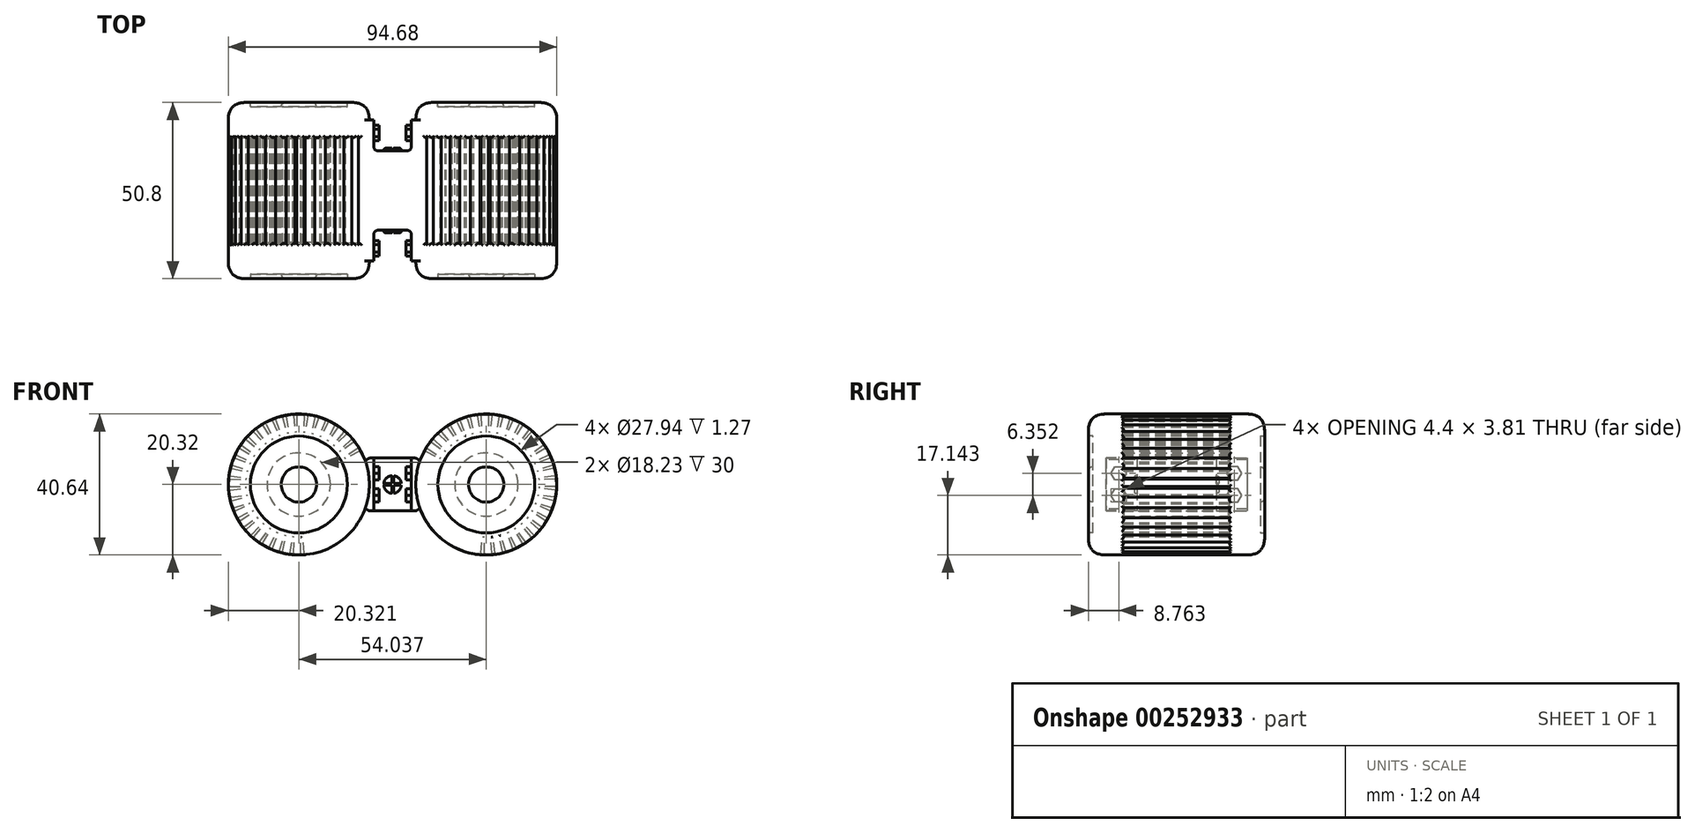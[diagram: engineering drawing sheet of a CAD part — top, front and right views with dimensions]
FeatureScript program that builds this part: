
annotation { "Feature Type Name" : "Feature", "Feature Type Description" : "" }
export const myFeature = defineFeature(function(context is Context, id is Id, definition is map)
    precondition{}
    {
        {
            var Q0;
            Q0=qCreatedBy(makeId("Front.planeOp"),FACE);
            var sketch = newSketch(context, id + "F0", { "sketchPlane" : qUnion([Q0])});
            skArc(sketch, "E0", {"start": v(26.53, 38.5) * mm, "mid": v(31.42, 78.66) * mm, "end": v(18.88, 40.2) * mm});
            skCircle(sketch, "E1", {"center": v(-27.02, 58.82) * mm, "radius": 20.32 * mm});
            skArc(sketch, "E2", {"start": v(18.88, 40.2) * mm, "mid": v(22.62, 38.98) * mm, "end": v(26.53, 38.5) * mm});
            skSolve(sketch);
        }
        {
            var Q0;
            Q0=qSketchRegion(id+"F0",true);
            extrude(context, id + "F1", {"entities" : qUnion([Q0]), "endBound" : BoundingType.SYMMETRIC, "depth" : 50.8 * mm});
        }
        {
            var Q0;
            Q0=qCreatedBy(makeId("Front.planeOp"),FACE);
            var sketch = newSketch(context, id + "F2", { "sketchPlane" : qUnion([Q0])});
            skLineSegment(sketch, "E3.1.0", {"start": v(13.83, 74.28) * mm, "end": v(17.03, 70.33) * mm});
            skLineSegment(sketch, "E3.1.1", {"start": v(13.07, 73.6) * mm, "end": v(16.65, 69.99) * mm});
            skLineSegment(sketch, "E3.1.2", {"start": v(13.07, 73.6) * mm, "end": v(13.83, 74.28) * mm});
            skLineSegment(sketch, "E3.1.3", {"start": v(16.65, 69.99) * mm, "end": v(17.03, 70.33) * mm, "construction": true});
            skLineSegment(sketch, "E3.1.4", {"start": v(16.65, 69.99) * mm, "end": v(17.03, 70.33) * mm});
            skPoint(sketch, "E4", {"position": v(27.02, 58.82) * mm});
            skPoint(sketch, "E5", {"position": v(-27.02, 58.82) * mm});
            skLineSegment(sketch, "E6", {"start": v(27.02, 58.82) * mm, "end": v(13.45, 73.94) * mm, "construction": true});
            skLineSegment(sketch, "E7.1.0", {"start": v(-13.07, 73.6) * mm, "end": v(-16.65, 69.99) * mm});
            skLineSegment(sketch, "E7.1.1", {"start": v(-13.83, 74.28) * mm, "end": v(-17.03, 70.33) * mm});
            skLineSegment(sketch, "E7.1.2", {"start": v(-13.83, 74.28) * mm, "end": v(-13.07, 73.6) * mm});
            skLineSegment(sketch, "E7.1.3", {"start": v(-17.03, 70.33) * mm, "end": v(-16.65, 69.99) * mm, "construction": true});
            skLineSegment(sketch, "E7.1.4", {"start": v(-17.03, 70.33) * mm, "end": v(-16.65, 69.99) * mm});
            skLineSegment(sketch, "E8", {"start": v(-27.02, 58.82) * mm, "end": v(-13.45, 73.94) * mm, "construction": true});
            skLineSegment(sketch, "E9.1.0", {"start": v(11.57, 72.03) * mm, "end": v(15.35, 68.63) * mm});
            skLineSegment(sketch, "E9.1.1", {"start": v(10.93, 71.24) * mm, "end": v(15.03, 68.23) * mm});
            skLineSegment(sketch, "E9.1.2", {"start": v(10.93, 71.24) * mm, "end": v(11.57, 72.03) * mm});
            skLineSegment(sketch, "E9.1.3", {"start": v(15.03, 68.23) * mm, "end": v(15.35, 68.63) * mm, "construction": true});
            skLineSegment(sketch, "E9.1.4", {"start": v(15.03, 68.23) * mm, "end": v(15.35, 68.63) * mm});
            skLineSegment(sketch, "E9.2.0", {"start": v(9.7, 69.45) * mm, "end": v(13.96, 66.68) * mm});
            skLineSegment(sketch, "E9.2.1", {"start": v(9.18, 68.57) * mm, "end": v(13.7, 66.24) * mm});
            skLineSegment(sketch, "E9.2.2", {"start": v(9.18, 68.57) * mm, "end": v(9.7, 69.45) * mm});
            skLineSegment(sketch, "E9.2.3", {"start": v(13.7, 66.24) * mm, "end": v(13.96, 66.68) * mm, "construction": true});
            skLineSegment(sketch, "E9.2.4", {"start": v(13.7, 66.24) * mm, "end": v(13.96, 66.68) * mm});
            skLineSegment(sketch, "E9.15.0", {"start": v(25.41, 38.55) * mm, "end": v(25.94, 43.62) * mm});
            skLineSegment(sketch, "E9.15.1", {"start": v(26.43, 38.5) * mm, "end": v(26.45, 43.59) * mm});
            skLineSegment(sketch, "E9.15.2", {"start": v(26.43, 38.5) * mm, "end": v(25.41, 38.55) * mm});
            skLineSegment(sketch, "E9.15.3", {"start": v(26.45, 43.59) * mm, "end": v(25.94, 43.62) * mm, "construction": true});
            skLineSegment(sketch, "E9.15.4", {"start": v(26.45, 43.59) * mm, "end": v(25.94, 43.62) * mm});
            skLineSegment(sketch, "E9.16.0", {"start": v(28.6, 38.55) * mm, "end": v(28.33, 43.63) * mm});
            skLineSegment(sketch, "E9.16.1", {"start": v(29.61, 38.66) * mm, "end": v(28.84, 43.69) * mm});
            skLineSegment(sketch, "E9.16.2", {"start": v(29.61, 38.66) * mm, "end": v(28.6, 38.55) * mm});
            skLineSegment(sketch, "E9.16.3", {"start": v(28.84, 43.69) * mm, "end": v(28.33, 43.63) * mm, "construction": true});
            skLineSegment(sketch, "E9.16.4", {"start": v(28.84, 43.69) * mm, "end": v(28.33, 43.63) * mm});
            skLineSegment(sketch, "E9.17.0", {"start": v(31.75, 39.05) * mm, "end": v(30.7, 44.03) * mm});
            skLineSegment(sketch, "E9.17.1", {"start": v(32.73, 39.31) * mm, "end": v(31.18, 44.16) * mm});
            skLineSegment(sketch, "E9.17.2", {"start": v(32.73, 39.31) * mm, "end": v(31.75, 39.05) * mm});
            skLineSegment(sketch, "E9.17.3", {"start": v(31.18, 44.16) * mm, "end": v(30.7, 44.03) * mm, "construction": true});
            skLineSegment(sketch, "E9.17.4", {"start": v(31.18, 44.16) * mm, "end": v(30.7, 44.03) * mm});
            skLineSegment(sketch, "E9.18.0", {"start": v(34.79, 40.03) * mm, "end": v(32.96, 44.78) * mm});
            skLineSegment(sketch, "E9.18.1", {"start": v(35.72, 40.45) * mm, "end": v(33.42, 44.99) * mm});
            skLineSegment(sketch, "E9.18.2", {"start": v(35.72, 40.45) * mm, "end": v(34.79, 40.03) * mm});
            skLineSegment(sketch, "E9.18.3", {"start": v(33.42, 44.99) * mm, "end": v(32.96, 44.78) * mm, "construction": true});
            skLineSegment(sketch, "E9.18.4", {"start": v(33.42, 44.99) * mm, "end": v(32.96, 44.78) * mm});
            skLineSegment(sketch, "E9.19.0", {"start": v(37.63, 41.48) * mm, "end": v(35.08, 45.89) * mm});
            skLineSegment(sketch, "E9.19.1", {"start": v(38.48, 42.03) * mm, "end": v(35.5, 46.16) * mm});
            skLineSegment(sketch, "E9.19.2", {"start": v(38.48, 42.03) * mm, "end": v(37.63, 41.48) * mm});
            skLineSegment(sketch, "E9.19.3", {"start": v(35.5, 46.16) * mm, "end": v(35.08, 45.89) * mm, "construction": true});
            skLineSegment(sketch, "E9.19.4", {"start": v(35.5, 46.16) * mm, "end": v(35.08, 45.89) * mm});
            skLineSegment(sketch, "E9.20.0", {"start": v(40.21, 43.35) * mm, "end": v(37, 47.3) * mm});
            skLineSegment(sketch, "E9.20.1", {"start": v(40.97, 44.03) * mm, "end": v(37.38, 47.65) * mm});
            skLineSegment(sketch, "E9.20.2", {"start": v(40.97, 44.03) * mm, "end": v(40.21, 43.35) * mm});
            skLineSegment(sketch, "E9.20.3", {"start": v(37.38, 47.65) * mm, "end": v(37, 47.3) * mm, "construction": true});
            skLineSegment(sketch, "E9.20.4", {"start": v(37.38, 47.65) * mm, "end": v(37, 47.3) * mm});
            skLineSegment(sketch, "E9.21.0", {"start": v(42.47, 45.6) * mm, "end": v(38.68, 49.01) * mm});
            skLineSegment(sketch, "E9.21.1", {"start": v(43.1, 46.4) * mm, "end": v(39, 49.4) * mm});
            skLineSegment(sketch, "E9.21.2", {"start": v(43.1, 46.4) * mm, "end": v(42.47, 45.6) * mm});
            skLineSegment(sketch, "E9.21.3", {"start": v(39, 49.4) * mm, "end": v(38.68, 49.01) * mm, "construction": true});
            skLineSegment(sketch, "E9.21.4", {"start": v(39, 49.4) * mm, "end": v(38.68, 49.01) * mm});
            skLineSegment(sketch, "E9.22.0", {"start": v(44.34, 48.19) * mm, "end": v(40.07, 50.96) * mm});
            skLineSegment(sketch, "E9.22.1", {"start": v(44.85, 49.07) * mm, "end": v(40.33, 51.4) * mm});
            skLineSegment(sketch, "E9.22.2", {"start": v(44.85, 49.07) * mm, "end": v(44.34, 48.19) * mm});
            skLineSegment(sketch, "E9.22.3", {"start": v(40.33, 51.4) * mm, "end": v(40.07, 50.96) * mm, "construction": true});
            skLineSegment(sketch, "E9.22.4", {"start": v(40.33, 51.4) * mm, "end": v(40.07, 50.96) * mm});
            skLineSegment(sketch, "E9.23.0", {"start": v(45.8, 51.03) * mm, "end": v(41.14, 53.1) * mm});
            skLineSegment(sketch, "E9.23.1", {"start": v(46.16, 51.98) * mm, "end": v(41.33, 53.57) * mm});
            skLineSegment(sketch, "E9.23.2", {"start": v(46.16, 51.98) * mm, "end": v(45.8, 51.03) * mm});
            skLineSegment(sketch, "E9.23.3", {"start": v(41.33, 53.57) * mm, "end": v(41.14, 53.1) * mm, "construction": true});
            skLineSegment(sketch, "E9.23.4", {"start": v(41.33, 53.57) * mm, "end": v(41.14, 53.1) * mm});
            skLineSegment(sketch, "E9.24.0", {"start": v(46.78, 54.06) * mm, "end": v(41.86, 55.37) * mm});
            skLineSegment(sketch, "E9.24.1", {"start": v(47, 55.05) * mm, "end": v(41.97, 55.87) * mm});
            skLineSegment(sketch, "E9.24.2", {"start": v(47, 55.05) * mm, "end": v(46.78, 54.06) * mm});
            skLineSegment(sketch, "E9.24.3", {"start": v(41.97, 55.87) * mm, "end": v(41.86, 55.37) * mm, "construction": true});
            skLineSegment(sketch, "E9.24.4", {"start": v(41.97, 55.87) * mm, "end": v(41.86, 55.37) * mm});
            skLineSegment(sketch, "E9.25.0", {"start": v(47.28, 57.21) * mm, "end": v(42.22, 57.74) * mm});
            skLineSegment(sketch, "E9.25.1", {"start": v(47.34, 58.23) * mm, "end": v(42.25, 58.25) * mm});
            skLineSegment(sketch, "E9.25.2", {"start": v(47.34, 58.23) * mm, "end": v(47.28, 57.21) * mm});
            skLineSegment(sketch, "E9.25.3", {"start": v(42.25, 58.25) * mm, "end": v(42.22, 57.74) * mm, "construction": true});
            skLineSegment(sketch, "E9.25.4", {"start": v(42.25, 58.25) * mm, "end": v(42.22, 57.74) * mm});
            skLineSegment(sketch, "E9.26.0", {"start": v(47.28, 60.4) * mm, "end": v(42.2, 60.13) * mm});
            skLineSegment(sketch, "E9.26.1", {"start": v(47.18, 61.41) * mm, "end": v(42.15, 60.64) * mm});
            skLineSegment(sketch, "E9.26.2", {"start": v(47.18, 61.41) * mm, "end": v(47.28, 60.4) * mm});
            skLineSegment(sketch, "E9.26.3", {"start": v(42.15, 60.64) * mm, "end": v(42.2, 60.13) * mm, "construction": true});
            skLineSegment(sketch, "E9.26.4", {"start": v(42.15, 60.64) * mm, "end": v(42.2, 60.13) * mm});
            skLineSegment(sketch, "E9.27.0", {"start": v(46.79, 63.55) * mm, "end": v(41.8, 62.5) * mm});
            skLineSegment(sketch, "E9.27.1", {"start": v(46.52, 64.53) * mm, "end": v(41.68, 62.98) * mm});
            skLineSegment(sketch, "E9.27.2", {"start": v(46.52, 64.53) * mm, "end": v(46.79, 63.55) * mm});
            skLineSegment(sketch, "E9.27.3", {"start": v(41.68, 62.98) * mm, "end": v(41.8, 62.5) * mm, "construction": true});
            skLineSegment(sketch, "E9.27.4", {"start": v(41.68, 62.98) * mm, "end": v(41.8, 62.5) * mm});
            skLineSegment(sketch, "E9.28.0", {"start": v(45.8, 66.59) * mm, "end": v(41.05, 64.76) * mm});
            skLineSegment(sketch, "E9.28.1", {"start": v(45.4, 67.51) * mm, "end": v(40.85, 65.22) * mm});
            skLineSegment(sketch, "E9.28.2", {"start": v(45.4, 67.51) * mm, "end": v(45.8, 66.59) * mm});
            skLineSegment(sketch, "E9.28.3", {"start": v(40.85, 65.22) * mm, "end": v(41.05, 64.76) * mm, "construction": true});
            skLineSegment(sketch, "E9.28.4", {"start": v(40.85, 65.22) * mm, "end": v(41.05, 64.76) * mm});
            skLineSegment(sketch, "E9.29.0", {"start": v(44.36, 69.43) * mm, "end": v(39.95, 66.88) * mm});
            skLineSegment(sketch, "E9.29.1", {"start": v(43.8, 70.28) * mm, "end": v(39.67, 67.3) * mm});
            skLineSegment(sketch, "E9.29.2", {"start": v(43.8, 70.28) * mm, "end": v(44.36, 69.43) * mm});
            skLineSegment(sketch, "E9.29.3", {"start": v(39.67, 67.3) * mm, "end": v(39.95, 66.88) * mm, "construction": true});
            skLineSegment(sketch, "E9.29.4", {"start": v(39.67, 67.3) * mm, "end": v(39.95, 66.88) * mm});
            skLineSegment(sketch, "E9.30.0", {"start": v(42.48, 72) * mm, "end": v(38.53, 68.8) * mm});
            skLineSegment(sketch, "E9.30.1", {"start": v(41.8, 72.77) * mm, "end": v(38.2, 69.18) * mm});
            skLineSegment(sketch, "E9.30.2", {"start": v(41.8, 72.77) * mm, "end": v(42.48, 72) * mm});
            skLineSegment(sketch, "E9.30.3", {"start": v(38.2, 69.18) * mm, "end": v(38.53, 68.8) * mm, "construction": true});
            skLineSegment(sketch, "E9.30.4", {"start": v(38.2, 69.18) * mm, "end": v(38.53, 68.8) * mm});
            skLineSegment(sketch, "E9.31.0", {"start": v(40.23, 74.27) * mm, "end": v(36.83, 70.48) * mm});
            skLineSegment(sketch, "E9.31.1", {"start": v(39.44, 74.9) * mm, "end": v(36.43, 70.8) * mm});
            skLineSegment(sketch, "E9.31.2", {"start": v(39.44, 74.9) * mm, "end": v(40.23, 74.27) * mm});
            skLineSegment(sketch, "E9.31.3", {"start": v(36.43, 70.8) * mm, "end": v(36.83, 70.48) * mm, "construction": true});
            skLineSegment(sketch, "E9.31.4", {"start": v(36.43, 70.8) * mm, "end": v(36.83, 70.48) * mm});
            skLineSegment(sketch, "E9.32.0", {"start": v(37.65, 76.14) * mm, "end": v(34.88, 71.87) * mm});
            skLineSegment(sketch, "E9.32.1", {"start": v(36.77, 76.65) * mm, "end": v(34.44, 72.13) * mm});
            skLineSegment(sketch, "E9.32.2", {"start": v(36.77, 76.65) * mm, "end": v(37.65, 76.14) * mm});
            skLineSegment(sketch, "E9.32.3", {"start": v(34.44, 72.13) * mm, "end": v(34.88, 71.87) * mm, "construction": true});
            skLineSegment(sketch, "E9.32.4", {"start": v(34.44, 72.13) * mm, "end": v(34.88, 71.87) * mm});
            skLineSegment(sketch, "E9.33.0", {"start": v(34.8, 77.6) * mm, "end": v(32.74, 72.94) * mm});
            skLineSegment(sketch, "E9.33.1", {"start": v(33.86, 77.96) * mm, "end": v(32.27, 73.13) * mm});
            skLineSegment(sketch, "E9.33.2", {"start": v(33.86, 77.96) * mm, "end": v(34.8, 77.6) * mm});
            skLineSegment(sketch, "E9.33.3", {"start": v(32.27, 73.13) * mm, "end": v(32.74, 72.94) * mm, "construction": true});
            skLineSegment(sketch, "E9.33.4", {"start": v(32.27, 73.13) * mm, "end": v(32.74, 72.94) * mm});
            skLineSegment(sketch, "E9.34.0", {"start": v(31.78, 78.58) * mm, "end": v(30.46, 73.66) * mm});
            skLineSegment(sketch, "E9.34.1", {"start": v(30.78, 78.8) * mm, "end": v(29.96, 73.77) * mm});
            skLineSegment(sketch, "E9.34.2", {"start": v(30.78, 78.8) * mm, "end": v(31.78, 78.58) * mm});
            skLineSegment(sketch, "E9.34.3", {"start": v(29.96, 73.77) * mm, "end": v(30.46, 73.66) * mm, "construction": true});
            skLineSegment(sketch, "E9.34.4", {"start": v(29.96, 73.77) * mm, "end": v(30.46, 73.66) * mm});
            skLineSegment(sketch, "E9.35.0", {"start": v(28.63, 79.08) * mm, "end": v(28.1, 74.02) * mm});
            skLineSegment(sketch, "E9.35.1", {"start": v(27.61, 79.14) * mm, "end": v(27.59, 74.05) * mm});
            skLineSegment(sketch, "E9.35.2", {"start": v(27.61, 79.14) * mm, "end": v(28.63, 79.08) * mm});
            skLineSegment(sketch, "E9.35.3", {"start": v(27.59, 74.05) * mm, "end": v(28.1, 74.02) * mm, "construction": true});
            skLineSegment(sketch, "E9.35.4", {"start": v(27.59, 74.05) * mm, "end": v(28.1, 74.02) * mm});
            skLineSegment(sketch, "E9.36.0", {"start": v(25.44, 79.08) * mm, "end": v(25.7, 74) * mm});
            skLineSegment(sketch, "E9.36.1", {"start": v(24.42, 78.98) * mm, "end": v(25.2, 73.95) * mm});
            skLineSegment(sketch, "E9.36.2", {"start": v(24.42, 78.98) * mm, "end": v(25.44, 79.08) * mm});
            skLineSegment(sketch, "E9.36.3", {"start": v(25.2, 73.95) * mm, "end": v(25.7, 74) * mm, "construction": true});
            skLineSegment(sketch, "E9.36.4", {"start": v(25.2, 73.95) * mm, "end": v(25.7, 74) * mm});
            skLineSegment(sketch, "E9.37.0", {"start": v(22.28, 78.59) * mm, "end": v(23.35, 73.6) * mm});
            skLineSegment(sketch, "E9.37.1", {"start": v(21.3, 78.32) * mm, "end": v(22.86, 73.48) * mm});
            skLineSegment(sketch, "E9.37.2", {"start": v(21.3, 78.32) * mm, "end": v(22.28, 78.59) * mm});
            skLineSegment(sketch, "E9.37.3", {"start": v(22.86, 73.48) * mm, "end": v(23.35, 73.6) * mm, "construction": true});
            skLineSegment(sketch, "E9.37.4", {"start": v(22.86, 73.48) * mm, "end": v(23.35, 73.6) * mm});
            skLineSegment(sketch, "E9.38.0", {"start": v(19.25, 77.6) * mm, "end": v(21.08, 72.85) * mm});
            skLineSegment(sketch, "E9.38.1", {"start": v(18.32, 77.19) * mm, "end": v(20.61, 72.65) * mm});
            skLineSegment(sketch, "E9.38.2", {"start": v(18.32, 77.19) * mm, "end": v(19.25, 77.6) * mm});
            skLineSegment(sketch, "E9.38.3", {"start": v(20.61, 72.65) * mm, "end": v(21.08, 72.85) * mm, "construction": true});
            skLineSegment(sketch, "E9.38.4", {"start": v(20.61, 72.65) * mm, "end": v(21.08, 72.85) * mm});
            skLineSegment(sketch, "E9.39.0", {"start": v(16.4, 76.15) * mm, "end": v(18.96, 71.75) * mm});
            skLineSegment(sketch, "E9.39.1", {"start": v(15.56, 75.6) * mm, "end": v(18.53, 71.47) * mm});
            skLineSegment(sketch, "E9.39.2", {"start": v(15.56, 75.6) * mm, "end": v(16.4, 76.15) * mm});
            skLineSegment(sketch, "E9.39.3", {"start": v(18.53, 71.47) * mm, "end": v(18.96, 71.75) * mm, "construction": true});
            skLineSegment(sketch, "E9.39.4", {"start": v(18.53, 71.47) * mm, "end": v(18.96, 71.75) * mm});
            skLineSegment(sketch, "E10.1.0", {"start": v(-15.56, 75.6) * mm, "end": v(-18.53, 71.47) * mm});
            skLineSegment(sketch, "E10.1.1", {"start": v(-16.4, 76.15) * mm, "end": v(-18.96, 71.75) * mm});
            skLineSegment(sketch, "E10.1.2", {"start": v(-16.4, 76.15) * mm, "end": v(-15.56, 75.6) * mm});
            skLineSegment(sketch, "E10.1.3", {"start": v(-18.96, 71.75) * mm, "end": v(-18.53, 71.47) * mm, "construction": true});
            skLineSegment(sketch, "E10.1.4", {"start": v(-18.96, 71.75) * mm, "end": v(-18.53, 71.47) * mm});
            skLineSegment(sketch, "E10.2.0", {"start": v(-18.32, 77.19) * mm, "end": v(-20.61, 72.65) * mm});
            skLineSegment(sketch, "E10.2.1", {"start": v(-19.25, 77.6) * mm, "end": v(-21.08, 72.85) * mm});
            skLineSegment(sketch, "E10.2.2", {"start": v(-19.25, 77.6) * mm, "end": v(-18.32, 77.19) * mm});
            skLineSegment(sketch, "E10.2.3", {"start": v(-21.08, 72.85) * mm, "end": v(-20.61, 72.65) * mm, "construction": true});
            skLineSegment(sketch, "E10.2.4", {"start": v(-21.08, 72.85) * mm, "end": v(-20.61, 72.65) * mm});
            skLineSegment(sketch, "E10.3.0", {"start": v(-21.3, 78.32) * mm, "end": v(-22.86, 73.48) * mm});
            skLineSegment(sketch, "E10.3.1", {"start": v(-22.28, 78.59) * mm, "end": v(-23.35, 73.6) * mm});
            skLineSegment(sketch, "E10.3.2", {"start": v(-22.28, 78.59) * mm, "end": v(-21.3, 78.32) * mm});
            skLineSegment(sketch, "E10.3.3", {"start": v(-23.35, 73.6) * mm, "end": v(-22.86, 73.48) * mm, "construction": true});
            skLineSegment(sketch, "E10.3.4", {"start": v(-23.35, 73.6) * mm, "end": v(-22.86, 73.48) * mm});
            skLineSegment(sketch, "E10.4.0", {"start": v(-24.42, 78.98) * mm, "end": v(-25.2, 73.95) * mm});
            skLineSegment(sketch, "E10.4.1", {"start": v(-25.44, 79.08) * mm, "end": v(-25.7, 74) * mm});
            skLineSegment(sketch, "E10.4.2", {"start": v(-25.44, 79.08) * mm, "end": v(-24.42, 78.98) * mm});
            skLineSegment(sketch, "E10.4.3", {"start": v(-25.7, 74) * mm, "end": v(-25.2, 73.95) * mm, "construction": true});
            skLineSegment(sketch, "E10.4.4", {"start": v(-25.7, 74) * mm, "end": v(-25.2, 73.95) * mm});
            skLineSegment(sketch, "E10.5.0", {"start": v(-27.61, 79.14) * mm, "end": v(-27.59, 74.05) * mm});
            skLineSegment(sketch, "E10.5.1", {"start": v(-28.63, 79.08) * mm, "end": v(-28.1, 74.02) * mm});
            skLineSegment(sketch, "E10.5.2", {"start": v(-28.63, 79.08) * mm, "end": v(-27.61, 79.14) * mm});
            skLineSegment(sketch, "E10.5.3", {"start": v(-28.1, 74.02) * mm, "end": v(-27.59, 74.05) * mm, "construction": true});
            skLineSegment(sketch, "E10.5.4", {"start": v(-28.1, 74.02) * mm, "end": v(-27.59, 74.05) * mm});
            skLineSegment(sketch, "E10.6.0", {"start": v(-30.78, 78.8) * mm, "end": v(-29.96, 73.77) * mm});
            skLineSegment(sketch, "E10.6.1", {"start": v(-31.78, 78.58) * mm, "end": v(-30.46, 73.66) * mm});
            skLineSegment(sketch, "E10.6.2", {"start": v(-31.78, 78.58) * mm, "end": v(-30.78, 78.8) * mm});
            skLineSegment(sketch, "E10.6.3", {"start": v(-30.46, 73.66) * mm, "end": v(-29.96, 73.77) * mm, "construction": true});
            skLineSegment(sketch, "E10.6.4", {"start": v(-30.46, 73.66) * mm, "end": v(-29.96, 73.77) * mm});
            skLineSegment(sketch, "E10.7.0", {"start": v(-33.86, 77.96) * mm, "end": v(-32.27, 73.13) * mm});
            skLineSegment(sketch, "E10.7.1", {"start": v(-34.8, 77.6) * mm, "end": v(-32.74, 72.94) * mm});
            skLineSegment(sketch, "E10.7.2", {"start": v(-34.8, 77.6) * mm, "end": v(-33.86, 77.96) * mm});
            skLineSegment(sketch, "E10.7.3", {"start": v(-32.74, 72.94) * mm, "end": v(-32.27, 73.13) * mm, "construction": true});
            skLineSegment(sketch, "E10.7.4", {"start": v(-32.74, 72.94) * mm, "end": v(-32.27, 73.13) * mm});
            skLineSegment(sketch, "E10.8.0", {"start": v(-36.77, 76.65) * mm, "end": v(-34.44, 72.13) * mm});
            skLineSegment(sketch, "E10.8.1", {"start": v(-37.65, 76.14) * mm, "end": v(-34.88, 71.87) * mm});
            skLineSegment(sketch, "E10.8.2", {"start": v(-37.65, 76.14) * mm, "end": v(-36.77, 76.65) * mm});
            skLineSegment(sketch, "E10.8.3", {"start": v(-34.88, 71.87) * mm, "end": v(-34.44, 72.13) * mm, "construction": true});
            skLineSegment(sketch, "E10.8.4", {"start": v(-34.88, 71.87) * mm, "end": v(-34.44, 72.13) * mm});
            skLineSegment(sketch, "E10.9.0", {"start": v(-39.44, 74.9) * mm, "end": v(-36.43, 70.8) * mm});
            skLineSegment(sketch, "E10.9.1", {"start": v(-40.23, 74.27) * mm, "end": v(-36.83, 70.48) * mm});
            skLineSegment(sketch, "E10.9.2", {"start": v(-40.23, 74.27) * mm, "end": v(-39.44, 74.9) * mm});
            skLineSegment(sketch, "E10.9.3", {"start": v(-36.83, 70.48) * mm, "end": v(-36.43, 70.8) * mm, "construction": true});
            skLineSegment(sketch, "E10.9.4", {"start": v(-36.83, 70.48) * mm, "end": v(-36.43, 70.8) * mm});
            skLineSegment(sketch, "E10.10.0", {"start": v(-41.8, 72.77) * mm, "end": v(-38.2, 69.18) * mm});
            skLineSegment(sketch, "E10.10.1", {"start": v(-42.48, 72) * mm, "end": v(-38.53, 68.8) * mm});
            skLineSegment(sketch, "E10.10.2", {"start": v(-42.48, 72) * mm, "end": v(-41.8, 72.77) * mm});
            skLineSegment(sketch, "E10.10.3", {"start": v(-38.53, 68.8) * mm, "end": v(-38.2, 69.18) * mm, "construction": true});
            skLineSegment(sketch, "E10.10.4", {"start": v(-38.53, 68.8) * mm, "end": v(-38.2, 69.18) * mm});
            skLineSegment(sketch, "E10.11.0", {"start": v(-43.8, 70.28) * mm, "end": v(-39.67, 67.3) * mm});
            skLineSegment(sketch, "E10.11.1", {"start": v(-44.36, 69.43) * mm, "end": v(-39.95, 66.88) * mm});
            skLineSegment(sketch, "E10.11.2", {"start": v(-44.36, 69.43) * mm, "end": v(-43.8, 70.28) * mm});
            skLineSegment(sketch, "E10.11.3", {"start": v(-39.95, 66.88) * mm, "end": v(-39.67, 67.3) * mm, "construction": true});
            skLineSegment(sketch, "E10.11.4", {"start": v(-39.95, 66.88) * mm, "end": v(-39.67, 67.3) * mm});
            skLineSegment(sketch, "E10.12.0", {"start": v(-45.4, 67.51) * mm, "end": v(-40.85, 65.22) * mm});
            skLineSegment(sketch, "E10.12.1", {"start": v(-45.8, 66.59) * mm, "end": v(-41.05, 64.76) * mm});
            skLineSegment(sketch, "E10.12.2", {"start": v(-45.8, 66.59) * mm, "end": v(-45.4, 67.51) * mm});
            skLineSegment(sketch, "E10.12.3", {"start": v(-41.05, 64.76) * mm, "end": v(-40.85, 65.22) * mm, "construction": true});
            skLineSegment(sketch, "E10.12.4", {"start": v(-41.05, 64.76) * mm, "end": v(-40.85, 65.22) * mm});
            skLineSegment(sketch, "E10.13.0", {"start": v(-46.52, 64.53) * mm, "end": v(-41.68, 62.98) * mm});
            skLineSegment(sketch, "E10.13.1", {"start": v(-46.79, 63.55) * mm, "end": v(-41.8, 62.5) * mm});
            skLineSegment(sketch, "E10.13.2", {"start": v(-46.79, 63.55) * mm, "end": v(-46.52, 64.53) * mm});
            skLineSegment(sketch, "E10.13.3", {"start": v(-41.8, 62.5) * mm, "end": v(-41.68, 62.98) * mm, "construction": true});
            skLineSegment(sketch, "E10.13.4", {"start": v(-41.8, 62.5) * mm, "end": v(-41.68, 62.98) * mm});
            skLineSegment(sketch, "E10.14.0", {"start": v(-47.18, 61.41) * mm, "end": v(-42.15, 60.64) * mm});
            skLineSegment(sketch, "E10.14.1", {"start": v(-47.28, 60.4) * mm, "end": v(-42.2, 60.13) * mm});
            skLineSegment(sketch, "E10.14.2", {"start": v(-47.28, 60.4) * mm, "end": v(-47.18, 61.41) * mm});
            skLineSegment(sketch, "E10.14.3", {"start": v(-42.2, 60.13) * mm, "end": v(-42.15, 60.64) * mm, "construction": true});
            skLineSegment(sketch, "E10.14.4", {"start": v(-42.2, 60.13) * mm, "end": v(-42.15, 60.64) * mm});
            skLineSegment(sketch, "E10.15.0", {"start": v(-47.34, 58.23) * mm, "end": v(-42.25, 58.25) * mm});
            skLineSegment(sketch, "E10.15.1", {"start": v(-47.28, 57.21) * mm, "end": v(-42.22, 57.74) * mm});
            skLineSegment(sketch, "E10.15.2", {"start": v(-47.28, 57.21) * mm, "end": v(-47.34, 58.23) * mm});
            skLineSegment(sketch, "E10.15.3", {"start": v(-42.22, 57.74) * mm, "end": v(-42.25, 58.25) * mm, "construction": true});
            skLineSegment(sketch, "E10.15.4", {"start": v(-42.22, 57.74) * mm, "end": v(-42.25, 58.25) * mm});
            skLineSegment(sketch, "E10.16.0", {"start": v(-47, 55.05) * mm, "end": v(-41.97, 55.87) * mm});
            skLineSegment(sketch, "E10.16.1", {"start": v(-46.78, 54.06) * mm, "end": v(-41.86, 55.37) * mm});
            skLineSegment(sketch, "E10.16.2", {"start": v(-46.78, 54.06) * mm, "end": v(-47, 55.05) * mm});
            skLineSegment(sketch, "E10.16.3", {"start": v(-41.86, 55.37) * mm, "end": v(-41.97, 55.87) * mm, "construction": true});
            skLineSegment(sketch, "E10.16.4", {"start": v(-41.86, 55.37) * mm, "end": v(-41.97, 55.87) * mm});
            skLineSegment(sketch, "E10.17.0", {"start": v(-46.16, 51.98) * mm, "end": v(-41.33, 53.57) * mm});
            skLineSegment(sketch, "E10.17.1", {"start": v(-45.8, 51.03) * mm, "end": v(-41.14, 53.1) * mm});
            skLineSegment(sketch, "E10.17.2", {"start": v(-45.8, 51.03) * mm, "end": v(-46.16, 51.98) * mm});
            skLineSegment(sketch, "E10.17.3", {"start": v(-41.14, 53.1) * mm, "end": v(-41.33, 53.57) * mm, "construction": true});
            skLineSegment(sketch, "E10.17.4", {"start": v(-41.14, 53.1) * mm, "end": v(-41.33, 53.57) * mm});
            skLineSegment(sketch, "E10.18.0", {"start": v(-44.85, 49.07) * mm, "end": v(-40.33, 51.4) * mm});
            skLineSegment(sketch, "E10.18.1", {"start": v(-44.34, 48.19) * mm, "end": v(-40.07, 50.96) * mm});
            skLineSegment(sketch, "E10.18.2", {"start": v(-44.34, 48.19) * mm, "end": v(-44.85, 49.07) * mm});
            skLineSegment(sketch, "E10.18.3", {"start": v(-40.07, 50.96) * mm, "end": v(-40.33, 51.4) * mm, "construction": true});
            skLineSegment(sketch, "E10.18.4", {"start": v(-40.07, 50.96) * mm, "end": v(-40.33, 51.4) * mm});
            skLineSegment(sketch, "E10.19.0", {"start": v(-43.1, 46.4) * mm, "end": v(-39, 49.4) * mm});
            skLineSegment(sketch, "E10.19.1", {"start": v(-42.47, 45.6) * mm, "end": v(-38.68, 49.01) * mm});
            skLineSegment(sketch, "E10.19.2", {"start": v(-42.47, 45.6) * mm, "end": v(-43.1, 46.4) * mm});
            skLineSegment(sketch, "E10.19.3", {"start": v(-38.68, 49.01) * mm, "end": v(-39, 49.4) * mm, "construction": true});
            skLineSegment(sketch, "E10.19.4", {"start": v(-38.68, 49.01) * mm, "end": v(-39, 49.4) * mm});
            skLineSegment(sketch, "E10.20.0", {"start": v(-40.97, 44.03) * mm, "end": v(-37.38, 47.65) * mm});
            skLineSegment(sketch, "E10.20.1", {"start": v(-40.21, 43.35) * mm, "end": v(-37, 47.3) * mm});
            skLineSegment(sketch, "E10.20.2", {"start": v(-40.21, 43.35) * mm, "end": v(-40.97, 44.03) * mm});
            skLineSegment(sketch, "E10.20.3", {"start": v(-37, 47.3) * mm, "end": v(-37.38, 47.65) * mm, "construction": true});
            skLineSegment(sketch, "E10.20.4", {"start": v(-37, 47.3) * mm, "end": v(-37.38, 47.65) * mm});
            skLineSegment(sketch, "E10.21.0", {"start": v(-38.48, 42.03) * mm, "end": v(-35.5, 46.16) * mm});
            skLineSegment(sketch, "E10.21.1", {"start": v(-37.63, 41.48) * mm, "end": v(-35.08, 45.89) * mm});
            skLineSegment(sketch, "E10.21.2", {"start": v(-37.63, 41.48) * mm, "end": v(-38.48, 42.03) * mm});
            skLineSegment(sketch, "E10.21.3", {"start": v(-35.08, 45.89) * mm, "end": v(-35.5, 46.16) * mm, "construction": true});
            skLineSegment(sketch, "E10.21.4", {"start": v(-35.08, 45.89) * mm, "end": v(-35.5, 46.16) * mm});
            skLineSegment(sketch, "E10.22.0", {"start": v(-35.72, 40.45) * mm, "end": v(-33.42, 44.99) * mm});
            skLineSegment(sketch, "E10.22.1", {"start": v(-34.79, 40.03) * mm, "end": v(-32.96, 44.78) * mm});
            skLineSegment(sketch, "E10.22.2", {"start": v(-34.79, 40.03) * mm, "end": v(-35.72, 40.45) * mm});
            skLineSegment(sketch, "E10.22.3", {"start": v(-32.96, 44.78) * mm, "end": v(-33.42, 44.99) * mm, "construction": true});
            skLineSegment(sketch, "E10.22.4", {"start": v(-32.96, 44.78) * mm, "end": v(-33.42, 44.99) * mm});
            skLineSegment(sketch, "E10.23.0", {"start": v(-32.73, 39.31) * mm, "end": v(-31.18, 44.16) * mm});
            skLineSegment(sketch, "E10.23.1", {"start": v(-31.75, 39.05) * mm, "end": v(-30.7, 44.03) * mm});
            skLineSegment(sketch, "E10.23.2", {"start": v(-31.75, 39.05) * mm, "end": v(-32.73, 39.31) * mm});
            skLineSegment(sketch, "E10.23.3", {"start": v(-30.7, 44.03) * mm, "end": v(-31.18, 44.16) * mm, "construction": true});
            skLineSegment(sketch, "E10.23.4", {"start": v(-30.7, 44.03) * mm, "end": v(-31.18, 44.16) * mm});
            skLineSegment(sketch, "E10.24.0", {"start": v(-29.61, 38.66) * mm, "end": v(-28.84, 43.69) * mm});
            skLineSegment(sketch, "E10.24.1", {"start": v(-28.6, 38.55) * mm, "end": v(-28.33, 43.63) * mm});
            skLineSegment(sketch, "E10.24.2", {"start": v(-28.6, 38.55) * mm, "end": v(-29.61, 38.66) * mm});
            skLineSegment(sketch, "E10.24.3", {"start": v(-28.33, 43.63) * mm, "end": v(-28.84, 43.69) * mm, "construction": true});
            skLineSegment(sketch, "E10.24.4", {"start": v(-28.33, 43.63) * mm, "end": v(-28.84, 43.69) * mm});
            skLineSegment(sketch, "E10.25.0", {"start": v(-26.43, 38.5) * mm, "end": v(-26.45, 43.59) * mm});
            skLineSegment(sketch, "E10.25.1", {"start": v(-25.41, 38.55) * mm, "end": v(-25.94, 43.62) * mm});
            skLineSegment(sketch, "E10.25.2", {"start": v(-25.41, 38.55) * mm, "end": v(-26.43, 38.5) * mm});
            skLineSegment(sketch, "E10.25.3", {"start": v(-25.94, 43.62) * mm, "end": v(-26.45, 43.59) * mm, "construction": true});
            skLineSegment(sketch, "E10.25.4", {"start": v(-25.94, 43.62) * mm, "end": v(-26.45, 43.59) * mm});
            skLineSegment(sketch, "E10.38.0", {"start": v(-9.18, 68.57) * mm, "end": v(-13.7, 66.24) * mm});
            skLineSegment(sketch, "E10.38.1", {"start": v(-9.7, 69.45) * mm, "end": v(-13.96, 66.68) * mm});
            skLineSegment(sketch, "E10.38.2", {"start": v(-9.7, 69.45) * mm, "end": v(-9.18, 68.57) * mm});
            skLineSegment(sketch, "E10.38.3", {"start": v(-13.96, 66.68) * mm, "end": v(-13.7, 66.24) * mm, "construction": true});
            skLineSegment(sketch, "E10.38.4", {"start": v(-13.96, 66.68) * mm, "end": v(-13.7, 66.24) * mm});
            skLineSegment(sketch, "E10.39.0", {"start": v(-10.93, 71.24) * mm, "end": v(-15.03, 68.23) * mm});
            skLineSegment(sketch, "E10.39.1", {"start": v(-11.57, 72.03) * mm, "end": v(-15.35, 68.63) * mm});
            skLineSegment(sketch, "E10.39.2", {"start": v(-11.57, 72.03) * mm, "end": v(-10.93, 71.24) * mm});
            skLineSegment(sketch, "E10.39.3", {"start": v(-15.35, 68.63) * mm, "end": v(-15.03, 68.23) * mm, "construction": true});
            skLineSegment(sketch, "E10.39.4", {"start": v(-15.35, 68.63) * mm, "end": v(-15.03, 68.23) * mm});
            skSolve(sketch);
        }
        {
            var Q0;
            Q0=qSketchRegion(id+"F2",true);
            extrude(context, id + "F3", {"entities" : qUnion([Q0]), "operationType" : NewBodyOperationType.REMOVE, "endBound" : BoundingType.SYMMETRIC, "oppositeDirection" : true, "depth" : 30.48 * mm});
        }
        {
            var Q0;
            Q0=makeQuery(id+"F1.opExtrude","CAP_EDGE",EDGE,{"disambiguationData":[OSD([sQuery(id+"F0.wireOp",EDGE,"E0")])],"isStart":false});
            var Q1;
            Q1=makeQuery(id+"F1.opExtrude","CAP_EDGE",EDGE,{"disambiguationData":[OSD([sQuery(id+"F0.wireOp",EDGE,"E0")])],"isStart":true});
            var Q2;
            Q2=makeQuery(id+"F1.opExtrude","CAP_EDGE",EDGE,{"disambiguationData":[OSD([sQuery(id+"F0.wireOp",EDGE,"eJ6pUaNj-pi6J-WJvS-oHvt-8XujmQXpYSx1")])],"isStart":true});
            var Q3;
            Q3=makeQuery(id+"F1.opExtrude","CAP_EDGE",EDGE,{"disambiguationData":[OSD([sQuery(id+"F0.wireOp",EDGE,"eJ6pUaNj-pi6J-WJvS-oHvt-8XujmQXpYSx1")])],"isStart":false});
            var Q4;
            Q4=makeQuery(id+"F1.opExtrude","CAP_EDGE",EDGE,{"disambiguationData":[OSD([sQuery(id+"F0.wireOp",EDGE,"E1")])],"isStart":false});
            var Q5;
            Q5=makeQuery(id+"F1.opExtrude","CAP_EDGE",EDGE,{"disambiguationData":[OSD([sQuery(id+"F0.wireOp",EDGE,"E1")])],"isStart":true});
            fillet(context, id + "F4", {"entities" : qUnion([Q0, Q1, Q2, Q3, Q4, Q5]), "radius" : 5.08 * mm, "tangentPropagation" : true, "rho" : 0.5, "crossSection" : FilletCrossSection.CONIC, "allowEdgeOverflow" : false});
        }
        {
            var Q0;
            Q0=makeQuery(id+"F1.opExtrude","CAP_FACE",FACE,{"disambiguationData":[OSD([sQuery(id+"F0.wireOp",EDGE,"E0"),sQuery(id+"F0.wireOp",EDGE,"E2")])],"isStart":false});
            var sketch = newSketch(context, id + "F5", { "sketchPlane" : qUnion([Q0])});
            skCircle(sketch, "E11", {"center": v(27.02, 58.82) * mm, "radius": 20.32 * mm, "construction": true});
            skCircle(sketch, "E12", {"center": v(-27.02, 58.82) * mm, "radius": 20.32 * mm, "construction": true});
            skCircle(sketch, "E13", {"center": v(-27.02, 58.82) * mm, "radius": 13.97 * mm});
            skCircle(sketch, "E14", {"center": v(27.02, 58.82) * mm, "radius": 13.97 * mm});
            skCircle(sketch, "E15", {"center": v(-27.02, 58.82) * mm, "radius": 5.08 * mm});
            skCircle(sketch, "E16", {"center": v(27.02, 58.82) * mm, "radius": 5.08 * mm});
            skSolve(sketch);
        }
        {
            var Q0;
            Q0=qSketchRegion(id+"F5",true);
            extrude(context, id + "F6", {"entities" : qUnion([Q0]), "operationType" : NewBodyOperationType.REMOVE, "oppositeDirection" : true, "depth" : 1.27 * mm});
        }
        {
            var Q0;
            Q0=makeQuery(id+"F1.opExtrude","CAP_FACE",FACE,{"disambiguationData":[OSD([sQuery(id+"F0.wireOp",EDGE,"E0"),sQuery(id+"F0.wireOp",EDGE,"E2")])],"isStart":true});
            var sketch = newSketch(context, id + "F7", { "sketchPlane" : qUnion([Q0])});
            skCircle(sketch, "E17", {"center": v(-27.02, 58.82) * mm, "radius": 20.32 * mm, "construction": true});
            skCircle(sketch, "E18", {"center": v(27.02, 58.82) * mm, "radius": 20.32 * mm, "construction": true});
            skCircle(sketch, "E19", {"center": v(27.02, 58.82) * mm, "radius": 13.97 * mm});
            skCircle(sketch, "E20", {"center": v(-27.02, 58.82) * mm, "radius": 13.97 * mm});
            skCircle(sketch, "E21", {"center": v(-27.02, 58.82) * mm, "radius": 5.08 * mm});
            skCircle(sketch, "E22", {"center": v(27.02, 58.82) * mm, "radius": 5.08 * mm});
            skSolve(sketch);
        }
        {
            var Q0;
            Q0=qSketchRegion(id+"F7",true);
            extrude(context, id + "F8", {"entities" : qUnion([Q0]), "operationType" : NewBodyOperationType.REMOVE, "oppositeDirection" : true, "depth" : 1.27 * mm});
        }
        {
            var Q0;
            Q0=makeQuery(id+"F6.boolean.opBoolean","COPY",EDGE,{"derivedFrom":makeQuery(id+"F6.opExtrude","CAP_EDGE",EDGE,{"disambiguationData":[OSD([sQuery(id+"F5.wireOp",EDGE,"E15")])],"isStart":true})});
            var Q1;
            Q1=makeQuery(id+"F6.boolean.opBoolean","COPY",EDGE,{"derivedFrom":makeQuery(id+"F6.opExtrude","CAP_EDGE",EDGE,{"disambiguationData":[OSD([sQuery(id+"F5.wireOp",EDGE,"E16")])],"isStart":true})});
            var Q2;
            Q2=makeQuery(id+"F8.boolean.opBoolean","COPY",EDGE,{"derivedFrom":makeQuery(id+"F8.opExtrude","CAP_EDGE",EDGE,{"disambiguationData":[OSD([sQuery(id+"F7.wireOp",EDGE,"E21")])],"isStart":true})});
            var Q3;
            Q3=makeQuery(id+"F8.boolean.opBoolean","COPY",EDGE,{"derivedFrom":makeQuery(id+"F8.opExtrude","CAP_EDGE",EDGE,{"disambiguationData":[OSD([sQuery(id+"F7.wireOp",EDGE,"E22")])],"isStart":true})});
            fillet(context, id + "F9", {"entities" : qUnion([Q0, Q1, Q2, Q3]), "radius" : 1.27 * mm, "tangentPropagation" : true, "allowEdgeOverflow" : false});
        }
        {
            var Q0;
            Q0=qCreatedBy(makeId("Front.planeOp"),FACE);
            var sketch = newSketch(context, id + "F10", { "sketchPlane" : qUnion([Q0])});
            skArc(sketch, "E23.0", {"start": v(7.6, 64.8) * mm, "mid": v(6.7, 58.82) * mm, "end": v(7.6, 52.84) * mm});
            skArc(sketch, "E23.1", {"start": v(-7.6, 52.84) * mm, "mid": v(-6.7, 58.82) * mm, "end": v(-7.6, 64.8) * mm});
            skLineSegment(sketch, "E24", {"start": v(-6.38, 51.2) * mm, "end": v(6.38, 51.2) * mm});
            skLineSegment(sketch, "E25", {"start": v(-6.38, 66.44) * mm, "end": v(6.38, 66.44) * mm});
            skPoint(sketch, "E26.visualSharp", {"position": v(-8.18, 66.44) * mm});
            skArc(sketch, "E26.filletArc", {"start": v(-6.38, 66.44) * mm, "mid": v(-7.4, 65.92) * mm, "end": v(-7.6, 64.8) * mm});
            skPoint(sketch, "E27.visualSharp", {"position": v(8.18, 66.44) * mm});
            skArc(sketch, "E27.filletArc", {"start": v(7.6, 64.8) * mm, "mid": v(7.4, 65.92) * mm, "end": v(6.38, 66.44) * mm});
            skPoint(sketch, "E28.visualSharp", {"position": v(8.18, 51.2) * mm});
            skArc(sketch, "E28.filletArc", {"start": v(6.38, 51.2) * mm, "mid": v(7.4, 51.71) * mm, "end": v(7.6, 52.84) * mm});
            skPoint(sketch, "E29.visualSharp", {"position": v(-8.18, 51.2) * mm});
            skArc(sketch, "E29.filletArc", {"start": v(-7.6, 52.84) * mm, "mid": v(-7.4, 51.71) * mm, "end": v(-6.38, 51.2) * mm});
            skSolve(sketch);
        }
        {
            var Q0;
            Q0=qSketchRegion(id+"F10",true);
            extrude(context, id + "F11", {"entities" : qUnion([Q0]), "depth" : 20.32 * mm});
        }
        {
            var Q0;
            Q0=makeQuery(id+"F11.opExtrude","CAP_FACE",FACE,{"disambiguationData":[OSD([sQuery(id+"F10.wireOp",EDGE,"E23.0"),sQuery(id+"F10.wireOp",EDGE,"E23.1"),sQuery(id+"F10.wireOp",EDGE,"E24"),sQuery(id+"F10.wireOp",EDGE,"E25"),sQuery(id+"F10.wireOp",EDGE,"E26.filletArc"),sQuery(id+"F10.wireOp",EDGE,"E27.filletArc"),sQuery(id+"F10.wireOp",EDGE,"E28.filletArc"),sQuery(id+"F10.wireOp",EDGE,"E29.filletArc")])],"isStart":false});
            var sketch = newSketch(context, id + "F12", { "sketchPlane" : qUnion([Q0])});
            skLineSegment(sketch, "E30.bottom", {"start": v(-5.43, 66.44) * mm, "end": v(5.43, 66.44) * mm});
            skLineSegment(sketch, "E30.top", {"start": v(-5.43, 51.2) * mm, "end": v(5.43, 51.2) * mm});
            skLineSegment(sketch, "E30.left", {"start": v(-5.43, 66.44) * mm, "end": v(-5.43, 51.2) * mm});
            skLineSegment(sketch, "E30.right", {"start": v(5.43, 66.44) * mm, "end": v(5.43, 51.2) * mm});
            skSolve(sketch);
        }
        {
            var Q0;
            Q0=qSketchRegion(id+"F12",true);
            extrude(context, id + "F13", {"entities" : qUnion([Q0]), "operationType" : NewBodyOperationType.REMOVE, "oppositeDirection" : true, "depth" : 8.9 * mm});
        }
        {
            var Q0;
            Q0=makeQuery(id+"F13.boolean.opBoolean","COPY",EDGE,{"derivedFrom":makeQuery(id+"F13.opExtrude","CAP_EDGE",EDGE,{"disambiguationData":[OSD([sQuery(id+"F12.wireOp",EDGE,"E30.left")])],"isStart":false})});
            var Q1;
            Q1=makeQuery(id+"F13.boolean.opBoolean","COPY",EDGE,{"derivedFrom":makeQuery(id+"F13.opExtrude","CAP_EDGE",EDGE,{"disambiguationData":[OSD([sQuery(id+"F12.wireOp",EDGE,"E30.right")])],"isStart":false})});
            fillet(context, id + "F14", {"entities" : qUnion([Q0, Q1]), "radius" : 1.27 * mm, "tangentPropagation" : true, "allowEdgeOverflow" : false});
        }
        {
            var Q0;
            Q0=makeQuery(id+"F13.boolean.opBoolean","COPY",FACE,{"derivedFrom":makeQuery(id+"F13.opExtrude","SWEPT_FACE",FACE,{"disambiguationData":[OSD([sQuery(id+"F12.wireOp",EDGE,"E30.left")])]})});
            var sketch = newSketch(context, id + "F15", { "sketchPlane" : qUnion([Q0])});
            skCircle(sketch, "E31", {"center": v(-16.64, 55.64) * mm, "radius": 1.9 * mm, "construction": true});
            skCircle(sketch, "E32.cCircle", {"center": v(-16.64, 62) * mm, "radius": 1.9 * mm, "construction": true});
            skLineSegment(sketch, "E32.0", {"start": v(-17.74, 63.9) * mm, "end": v(-15.54, 63.9) * mm});
            skLineSegment(sketch, "E32.1", {"start": v(-15.54, 63.9) * mm, "end": v(-14.44, 62) * mm});
            skLineSegment(sketch, "E32.2", {"start": v(-14.44, 62) * mm, "end": v(-15.54, 60.09) * mm});
            skLineSegment(sketch, "E32.3", {"start": v(-15.54, 60.09) * mm, "end": v(-17.74, 60.09) * mm});
            skLineSegment(sketch, "E32.4", {"start": v(-17.74, 60.09) * mm, "end": v(-18.84, 62) * mm});
            skLineSegment(sketch, "E32.5", {"start": v(-18.84, 62) * mm, "end": v(-17.74, 63.9) * mm});
            skPoint(sketch, "E32.0.midPoint", {"position": v(-16.64, 63.9) * mm});
            skLineSegment(sketch, "E33.0", {"start": v(-17.74, 57.55) * mm, "end": v(-15.54, 57.55) * mm});
            skLineSegment(sketch, "E33.1", {"start": v(-15.54, 57.55) * mm, "end": v(-14.44, 55.64) * mm});
            skLineSegment(sketch, "E33.2", {"start": v(-14.44, 55.64) * mm, "end": v(-15.54, 53.74) * mm});
            skLineSegment(sketch, "E33.3", {"start": v(-15.54, 53.74) * mm, "end": v(-17.74, 53.74) * mm});
            skLineSegment(sketch, "E33.4", {"start": v(-17.74, 53.74) * mm, "end": v(-18.84, 55.64) * mm});
            skLineSegment(sketch, "E33.5", {"start": v(-18.84, 55.64) * mm, "end": v(-17.74, 57.55) * mm});
            skPoint(sketch, "E33.0.midPoint", {"position": v(-16.64, 57.55) * mm});
            skSolve(sketch);
        }
        {
            var Q0;
            Q0=qSketchRegion(id+"F15",true);
            extrude(context, id + "F16", {"entities" : qUnion([Q0]), "depth" : 1.52 * mm});
        }
        {
            var Q0;
            Q0=makeQuery(id+"F16.opExtrude","SWEPT_BODY",BODY,{"disambiguationData":[OSD([sQuery(id+"F15.wireOp",EDGE,"E32.0"),sQuery(id+"F15.wireOp",EDGE,"E32.1"),sQuery(id+"F15.wireOp",EDGE,"E32.2"),sQuery(id+"F15.wireOp",EDGE,"E32.3"),sQuery(id+"F15.wireOp",EDGE,"E32.4"),sQuery(id+"F15.wireOp",EDGE,"E32.5")])]});
            var Q1;
            Q1=makeQuery(id+"F16.opExtrude","SWEPT_BODY",BODY,{"disambiguationData":[OSD([sQuery(id+"F15.wireOp",EDGE,"E33.0"),sQuery(id+"F15.wireOp",EDGE,"E33.1"),sQuery(id+"F15.wireOp",EDGE,"E33.2"),sQuery(id+"F15.wireOp",EDGE,"E33.3"),sQuery(id+"F15.wireOp",EDGE,"E33.4"),sQuery(id+"F15.wireOp",EDGE,"E33.5")])]});
            var Q2;
            Q2=qCreatedBy(makeId("Right.planeOp"),FACE);
            mirror(context, id + "F17", {"operationType" : NewBodyOperationType.ADD, "entities" : qUnion([Q0, Q1]), "mirrorPlane" : qUnion([Q2])});
        }
        {
            var Q0;
            Q0=makeQuery(id+"F13.boolean.opBoolean","COPY",FACE,{"derivedFrom":makeQuery(id+"F13.opExtrude","CAP_FACE",FACE,{"disambiguationData":[OSD([sQuery(id+"F12.wireOp",EDGE,"E30.bottom"),sQuery(id+"F12.wireOp",EDGE,"E30.top"),sQuery(id+"F12.wireOp",EDGE,"E30.left"),sQuery(id+"F12.wireOp",EDGE,"E30.right")])],"isStart":false})});
            var sketch = newSketch(context, id + "F18", { "sketchPlane" : qUnion([Q0])});
            skArc(sketch, "E34", {"start": v(-0.25, 61.34) * mm, "mid": v(-1.8, 60.61) * mm, "end": v(-2.53, 59.07) * mm});
            skLineSegment(sketch, "E35.left", {"start": v(-0.25, 61.36) * mm, "end": v(-0.25, 59.07) * mm});
            skLineSegment(sketch, "E35.right", {"start": v(0.25, 61.36) * mm, "end": v(0.25, 59.07) * mm});
            skLineSegment(sketch, "E36.bottom", {"start": v(-2.54, 59.07) * mm, "end": v(-0.25, 59.07) * mm});
            skLineSegment(sketch, "E36.top", {"start": v(-2.54, 58.56) * mm, "end": v(-0.25, 58.56) * mm});
            skLineSegment(sketch, "E37.trimOffspring", {"start": v(0.25, 59.07) * mm, "end": v(2.54, 59.07) * mm});
            skLineSegment(sketch, "E38.trimOffspring", {"start": v(0.25, 58.56) * mm, "end": v(2.54, 58.56) * mm});
            skLineSegment(sketch, "E39.trimOffspring", {"start": v(-0.25, 58.56) * mm, "end": v(-0.25, 56.28) * mm});
            skLineSegment(sketch, "E40.trimOffspring", {"start": v(0.25, 58.56) * mm, "end": v(0.25, 56.28) * mm});
            skArc(sketch, "E41.trimOffspring", {"start": v(-2.53, 58.56) * mm, "mid": v(-1.8, 57.02) * mm, "end": v(-0.25, 56.3) * mm});
            skArc(sketch, "E42.trimOffspring", {"start": v(2.53, 59.07) * mm, "mid": v(1.8, 60.61) * mm, "end": v(0.25, 61.34) * mm});
            skArc(sketch, "E43.trimOffspring", {"start": v(0.25, 56.3) * mm, "mid": v(1.8, 57.02) * mm, "end": v(2.53, 58.56) * mm});
            skSolve(sketch);
        }
        {
            var Q0;
            Q0=qSketchRegion(id+"F18",true);
            extrude(context, id + "F19", {"entities" : qUnion([Q0]), "operationType" : NewBodyOperationType.ADD, "depth" : 0.76 * mm});
        }
        {
            var Q0;
            Q0=makeQuery(id+"F19.opExtrude","CAP_EDGE",EDGE,{"disambiguationData":[OSD([sQuery(id+"F18.wireOp",EDGE,"E42.trimOffspring")])],"isStart":false});
            var Q1;
            Q1=makeQuery(id+"F19.opExtrude","CAP_EDGE",EDGE,{"disambiguationData":[OSD([sQuery(id+"F18.wireOp",EDGE,"E34")])],"isStart":false});
            var Q2;
            Q2=makeQuery(id+"F19.opExtrude","CAP_EDGE",EDGE,{"disambiguationData":[OSD([sQuery(id+"F18.wireOp",EDGE,"E41.trimOffspring")])],"isStart":false});
            var Q3;
            Q3=makeQuery(id+"F19.opExtrude","CAP_EDGE",EDGE,{"disambiguationData":[OSD([sQuery(id+"F18.wireOp",EDGE,"E43.trimOffspring")])],"isStart":false});
            fillet(context, id + "F20", {"entities" : qUnion([Q0, Q1, Q2, Q3]), "radius" : 0.5 * mm, "tangentPropagation" : true, "allowEdgeOverflow" : false});
        }
        {
            var Q0;
            Q0=makeQuery(id+"F11.opExtrude","SWEPT_BODY",BODY,{"disambiguationData":[OSD([sQuery(id+"F10.wireOp",EDGE,"E23.0"),sQuery(id+"F10.wireOp",EDGE,"E23.1"),sQuery(id+"F10.wireOp",EDGE,"E24"),sQuery(id+"F10.wireOp",EDGE,"E25"),sQuery(id+"F10.wireOp",EDGE,"E26.filletArc"),sQuery(id+"F10.wireOp",EDGE,"E27.filletArc"),sQuery(id+"F10.wireOp",EDGE,"E28.filletArc"),sQuery(id+"F10.wireOp",EDGE,"E29.filletArc")])]});
            var Q1;
            Q1=makeQuery(id+"F1.opExtrude","SWEPT_BODY",BODY,{"disambiguationData":[OSD([sQuery(id+"F0.wireOp",EDGE,"E1")])]});
            var Q2;
            Q2=qCreatedBy(makeId("Front.planeOp"),FACE);
            mirror(context, id + "F21", {"operationType" : NewBodyOperationType.ADD, "entities" : qUnion([Q0, Q1]), "mirrorPlane" : qUnion([Q2])});
        }
        {
            var Q0;
            Q0=qCreatedBy(makeId("Front.planeOp"),FACE);
            var sketch = newSketch(context, id + "F22", { "sketchPlane" : qUnion([Q0])});
            skLineSegment(sketch, "E44", {"start": v(0, 58.82) * mm, "end": v(0, 0) * mm, "construction": true});
            skSolve(sketch);
        }
        {
            var Q0;
            Q0=makeQuery(id+"F1.opExtrude","SWEPT_BODY",BODY,{"disambiguationData":[OSD([sQuery(id+"F0.wireOp",EDGE,"E0"),sQuery(id+"F0.wireOp",EDGE,"E2")])]});
            var Q1;
            Q1=sQuery(id+"F22.wireOp",EDGE,"E44");
            transform(context, id + "F23", {"entities" : qUnion([Q0]), "transformType" : TransformType.TRANSLATION_ENTITY, "oppositeDirectionEntity" : false, "transformLine" : qUnion([Q1]), "makeCopy" : false});
        }
        {
            var Q0;
            Q0=qCreatedBy(makeId("Front.planeOp"),FACE);
            var sketch = newSketch(context, id + "F24", { "sketchPlane" : qUnion([Q0])});
            skCircle(sketch, "E45", {"center": v(-27.02, 0) * mm, "radius": 9.11 * mm});
            skCircle(sketch, "E46.MirrorC", {"center": v(27.02, 0) * mm, "radius": 9.11 * mm});
            skSolve(sketch);
        }
        {
            var Q0;
            Q0 = qSketchRegion(id + "F24", true);
            extrude(context, id + "F25", {"entities" : qUnion([Q0]), "operationType" : NewBodyOperationType.REMOVE, "endBound" : BoundingType.SYMMETRIC, "depth" : 30 * mm});
        }
        {
            var Q0;
            Q0=makeQuery(id+"F1.opExtrude","SWEPT_FACE",FACE,{"disambiguationData":[OSD([sQuery(id+"F0.wireOp",EDGE,"E0"),sQuery(id+"F0.wireOp",EDGE,"E2")])]});
            var Q1;
            Q1=makeQuery(id+"F1.opExtrude","SWEPT_FACE",FACE,{"disambiguationData":[OSD([sQuery(id+"F0.wireOp",EDGE,"E1")])]});
            fillet(context, id + "F26", {"entities" : qUnion([Q0, Q1]), "radius" : 0.5 * mm, "tangentPropagation" : true, "allowEdgeOverflow" : false});
        }
    });
